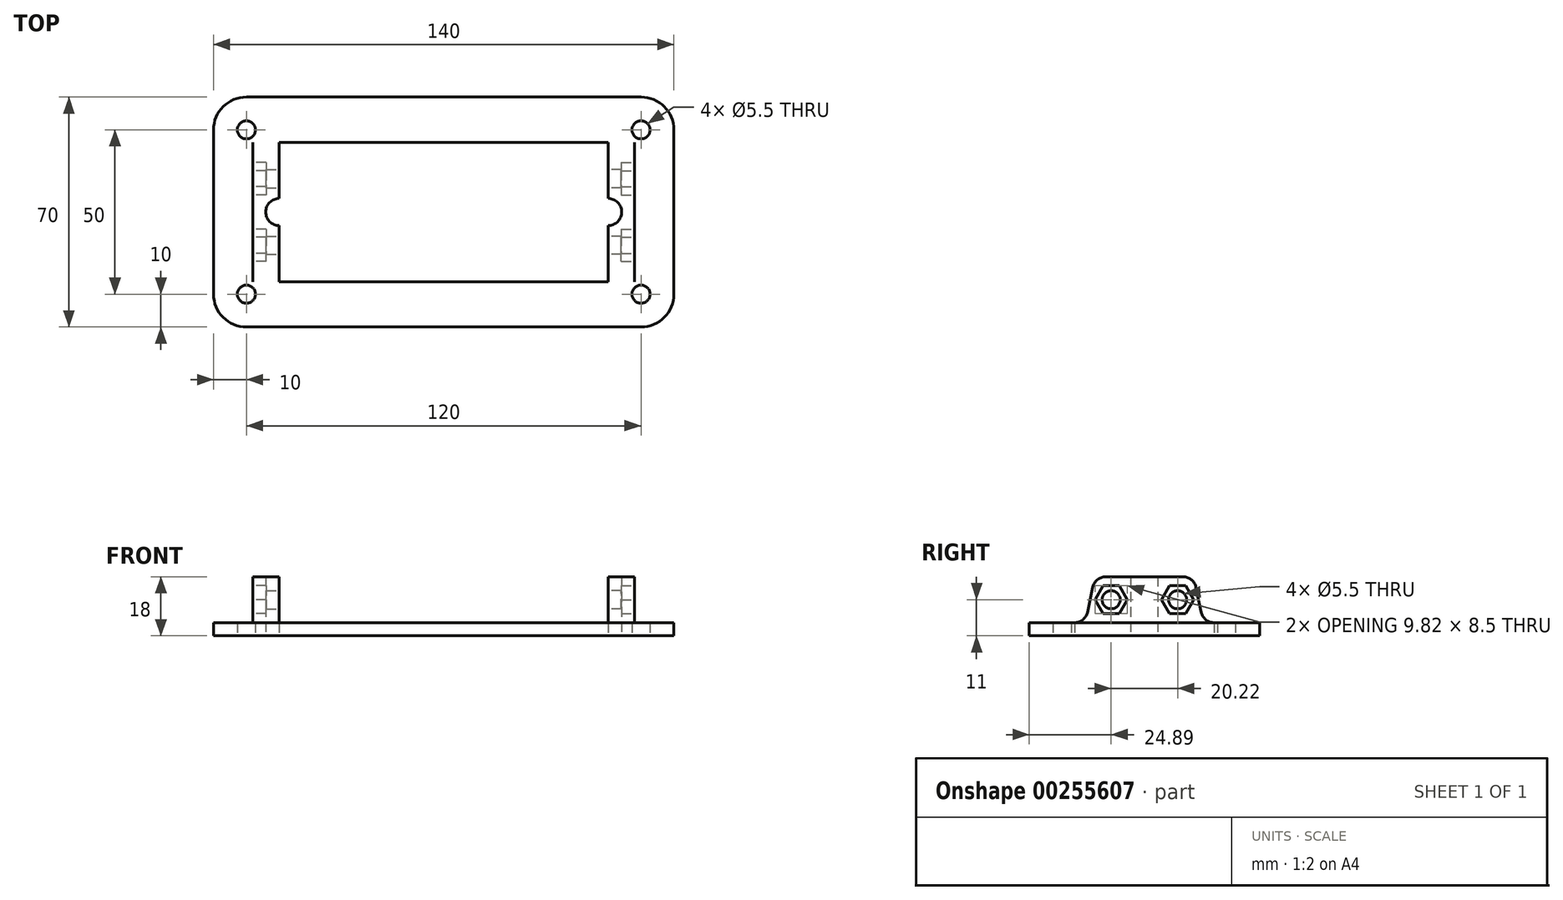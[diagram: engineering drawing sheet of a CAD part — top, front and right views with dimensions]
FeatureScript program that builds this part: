
annotation { "Feature Type Name" : "Feature", "Feature Type Description" : "" }
export const myFeature = defineFeature(function(context is Context, id is Id, definition is map)
    precondition{}
    {
        {
            var Q0;
            Q0=qCreatedBy(makeId("Top.planeOp"),FACE);
            var sketch = newSketch(context, id + "F0", { "sketchPlane" : qUnion([Q0])});
            skLineSegment(sketch, "E0.bottom", {"start": v(60, 35) * mm, "end": v(-60, 35) * mm});
            skLineSegment(sketch, "E0.top", {"start": v(60, -35) * mm, "end": v(-60, -35) * mm});
            skLineSegment(sketch, "E0.left", {"start": v(70, 25) * mm, "end": v(70, -25) * mm});
            skLineSegment(sketch, "E0.right", {"start": v(-70, 25) * mm, "end": v(-70, -25) * mm});
            skPoint(sketch, "E0.middle", {"position": v(0, 0) * mm});
            skLineSegment(sketch, "E1.bottom", {"start": v(50, 21.23) * mm, "end": v(-50, 21.23) * mm});
            skLineSegment(sketch, "E1.top", {"start": v(50, -21.23) * mm, "end": v(-50, -21.23) * mm});
            skLineSegment(sketch, "E1.left", {"start": v(50, 21.23) * mm, "end": v(50, -21.23) * mm});
            skLineSegment(sketch, "E1.right", {"start": v(-50, 21.23) * mm, "end": v(-50, -21.23) * mm});
            skLineSegment(sketch, "E2.bottom", {"start": v(-60, 25) * mm, "end": v(60, 25) * mm, "construction": true});
            skLineSegment(sketch, "E2.top", {"start": v(-60, -25) * mm, "end": v(60, -25) * mm, "construction": true});
            skLineSegment(sketch, "E2.left", {"start": v(-60, 25) * mm, "end": v(-60, -25) * mm, "construction": true});
            skLineSegment(sketch, "E2.right", {"start": v(60, 25) * mm, "end": v(60, -25) * mm, "construction": true});
            skCircle(sketch, "E3", {"center": v(-60, 25) * mm, "radius": 2.75 * mm});
            skCircle(sketch, "E4", {"center": v(60, 25) * mm, "radius": 2.75 * mm});
            skCircle(sketch, "E5", {"center": v(60, -25) * mm, "radius": 2.75 * mm});
            skCircle(sketch, "E6", {"center": v(-60, -25) * mm, "radius": 2.75 * mm});
            skPoint(sketch, "E7.visualSharp", {"position": v(-70, 35) * mm});
            skArc(sketch, "E7.filletArc", {"start": v(-60, 35) * mm, "mid": v(-67.07, 32.07) * mm, "end": v(-70, 25) * mm});
            skPoint(sketch, "E8.visualSharp", {"position": v(-70, -35) * mm});
            skArc(sketch, "E8.filletArc", {"start": v(-70, -25) * mm, "mid": v(-67.07, -32.07) * mm, "end": v(-60, -35) * mm});
            skPoint(sketch, "E9.visualSharp", {"position": v(70, -35) * mm});
            skArc(sketch, "E9.filletArc", {"start": v(60, -35) * mm, "mid": v(67.07, -32.07) * mm, "end": v(70, -25) * mm});
            skPoint(sketch, "E10.visualSharp", {"position": v(70, 35) * mm});
            skArc(sketch, "E10.filletArc", {"start": v(70, 25) * mm, "mid": v(67.07, 32.07) * mm, "end": v(60, 35) * mm});
            skSolve(sketch);
        }
        {
            var Q0;
            Q0=makeQuery(id+"F0.imprint","IMPRINT",FACE,{"disambiguationData":[TD([[makeQuery(id+"F0.imprint","IMPRINT",EDGE,{"derivedFrom":sQuery(id+"F0.wireOp",EDGE,"E0.bottom")}),1.0]])]});
            extrude(context, id + "F1", {"entities" : qUnion([Q0]), "depth" : 4 * mm});
        }
        {
            var Q0;
            Q0=makeQuery(id+"F1.opExtrude","SWEPT_FACE",FACE,{"disambiguationData":[OSD([sQuery(id+"F0.wireOp",EDGE,"E1.right")])]});
            var sketch = newSketch(context, id + "F2", { "sketchPlane" : qUnion([Q0])});
            skCircle(sketch, "E11", {"center": v(-10.11, 11) * mm, "radius": 2.75 * mm});
            skCircle(sketch, "E12.MirrorC", {"center": v(10.11, 11) * mm, "radius": 2.75 * mm});
            skArc(sketch, "E13", {"start": v(-21.24, 4) * mm, "mid": v(-18.72, 4.89) * mm, "end": v(-17.32, 7.16) * mm});
            skArc(sketch, "E14", {"start": v(-11.77, 18) * mm, "mid": v(-14.28, 17.11) * mm, "end": v(-15.68, 14.84) * mm});
            skLineSegment(sketch, "E15", {"start": v(-17.32, 7.16) * mm, "end": v(-15.68, 14.84) * mm});
            skLineSegment(sketch, "E16", {"start": v(-11.77, 18) * mm, "end": v(11.77, 18) * mm});
            skArc(sketch, "E17.MirrorCS", {"start": v(21.23, 4) * mm, "mid": v(18.72, 4.89) * mm, "end": v(17.32, 7.16) * mm});
            skLineSegment(sketch, "E18.MirrorCS", {"start": v(17.32, 7.16) * mm, "end": v(15.68, 14.84) * mm});
            skArc(sketch, "E19.MirrorCS", {"start": v(11.77, 18) * mm, "mid": v(14.28, 17.11) * mm, "end": v(15.68, 14.84) * mm});
            skSolve(sketch);
        }
        {
            var Q0;
            Q0=makeQuery(id+"F2.imprint","IMPRINT",FACE,{"disambiguationData":[TD([[makeQuery(id+"F2.imprint","IMPRINT",EDGE,{"derivedFrom":sQuery(id+"F2.wireOp",EDGE,"E11")}),-1.0]])]});
            extrude(context, id + "F3", {"entities" : qUnion([Q0]), "oppositeDirection" : true, "depth" : 8 * mm});
        }
        {
            var Q0;
            Q0=makeQuery(id+"F3.opExtrude","CAP_FACE",FACE,{"disambiguationData":[OSD([sQuery(id+"F0.wireOp",EDGE,"E1.right"),sQuery(id+"F2.wireOp",EDGE,"E11"),sQuery(id+"F2.wireOp",EDGE,"E12.MirrorC"),sQuery(id+"F2.wireOp",EDGE,"E13"),sQuery(id+"F2.wireOp",EDGE,"E14"),sQuery(id+"F2.wireOp",EDGE,"E15"),sQuery(id+"F2.wireOp",EDGE,"E16"),sQuery(id+"F2.wireOp",EDGE,"E17.MirrorCS"),sQuery(id+"F2.wireOp",EDGE,"E18.MirrorCS"),sQuery(id+"F2.wireOp",EDGE,"E19.MirrorCS")])],"isStart":false});
            var sketch = newSketch(context, id + "F4", { "sketchPlane" : qUnion([Q0])});
            skCircle(sketch, "E20.cCircle", {"center": v(-10.11, 11) * mm, "radius": 4.25 * mm, "construction": true});
            skLineSegment(sketch, "E20.0", {"start": v(-7.66, 15.25) * mm, "end": v(-5.2, 11) * mm});
            skLineSegment(sketch, "E20.1", {"start": v(-5.2, 11) * mm, "end": v(-7.66, 6.75) * mm});
            skLineSegment(sketch, "E20.2", {"start": v(-7.66, 6.75) * mm, "end": v(-12.56, 6.75) * mm});
            skLineSegment(sketch, "E20.3", {"start": v(-12.56, 6.75) * mm, "end": v(-15.02, 11) * mm});
            skLineSegment(sketch, "E20.4", {"start": v(-15.02, 11) * mm, "end": v(-12.56, 15.25) * mm});
            skLineSegment(sketch, "E20.5", {"start": v(-12.56, 15.25) * mm, "end": v(-7.66, 15.25) * mm});
            skPoint(sketch, "E20.0.midPoint", {"position": v(-6.43, 13.13) * mm});
            skCircle(sketch, "E21.cCircle", {"center": v(10.11, 11) * mm, "radius": 4.25 * mm, "construction": true});
            skLineSegment(sketch, "E21.0", {"start": v(12.56, 6.75) * mm, "end": v(7.66, 6.75) * mm});
            skLineSegment(sketch, "E21.1", {"start": v(7.66, 6.75) * mm, "end": v(5.2, 11) * mm});
            skLineSegment(sketch, "E21.2", {"start": v(5.2, 11) * mm, "end": v(7.66, 15.25) * mm});
            skLineSegment(sketch, "E21.3", {"start": v(7.66, 15.25) * mm, "end": v(12.56, 15.25) * mm});
            skLineSegment(sketch, "E21.4", {"start": v(12.56, 15.25) * mm, "end": v(15.02, 11) * mm});
            skLineSegment(sketch, "E21.5", {"start": v(15.02, 11) * mm, "end": v(12.56, 6.75) * mm});
            skPoint(sketch, "E21.0.midPoint", {"position": v(10.11, 6.75) * mm});
            skSolve(sketch);
        }
        {
            var Q0;
            Q0=makeQuery(id+"F4.imprint","IMPRINT",FACE,{"disambiguationData":[TD([[makeQuery(id+"F4.imprint","IMPRINT",EDGE,{"derivedFrom":sQuery(id+"F4.wireOp",EDGE,"E20.0")}),-1.0]])]});
            var Q1;
            Q1=makeQuery(id+"F4.imprint","IMPRINT",FACE,{"disambiguationData":[TD([[makeQuery(id+"F4.imprint","IMPRINT",EDGE,{"derivedFrom":sQuery(id+"F4.wireOp",EDGE,"E21.0")}),-1.0]])]});
            extrude(context, id + "F5", {"entities" : qUnion([Q0, Q1]), "operationType" : NewBodyOperationType.REMOVE, "oppositeDirection" : true, "depth" : 4 * mm});
        }
        {
            var Q0;
            Q0=makeQuery(id+"F3.opExtrude","SWEPT_BODY",BODY,{"disambiguationData":[OSD([sQuery(id+"F0.wireOp",EDGE,"E1.right"),sQuery(id+"F2.wireOp",EDGE,"E11"),sQuery(id+"F2.wireOp",EDGE,"E12.MirrorC"),sQuery(id+"F2.wireOp",EDGE,"E13"),sQuery(id+"F2.wireOp",EDGE,"E14"),sQuery(id+"F2.wireOp",EDGE,"E15"),sQuery(id+"F2.wireOp",EDGE,"E16"),sQuery(id+"F2.wireOp",EDGE,"E17.MirrorCS"),sQuery(id+"F2.wireOp",EDGE,"E18.MirrorCS"),sQuery(id+"F2.wireOp",EDGE,"E19.MirrorCS")])]});
            var Q1;
            Q1=qCreatedBy(makeId("Right.planeOp"),FACE);
            mirror(context, id + "F6", {"operationType" : NewBodyOperationType.ADD, "entities" : qUnion([Q0]), "mirrorPlane" : qUnion([Q1])});
        }
        {
            var Q0;
            Q0=makeQuery(id+"F1.opExtrude","CAP_FACE",FACE,{"disambiguationData":[OSD([sQuery(id+"F0.wireOp",EDGE,"E0.bottom"),sQuery(id+"F0.wireOp",EDGE,"E0.top"),sQuery(id+"F0.wireOp",EDGE,"E0.left"),sQuery(id+"F0.wireOp",EDGE,"E0.right"),sQuery(id+"F0.wireOp",EDGE,"E1.bottom"),sQuery(id+"F0.wireOp",EDGE,"E1.top"),sQuery(id+"F0.wireOp",EDGE,"E1.left"),sQuery(id+"F0.wireOp",EDGE,"E1.right"),sQuery(id+"F0.wireOp",EDGE,"E3"),sQuery(id+"F0.wireOp",EDGE,"E4"),sQuery(id+"F0.wireOp",EDGE,"E5"),sQuery(id+"F0.wireOp",EDGE,"E6"),sQuery(id+"F0.wireOp",EDGE,"E7.filletArc"),sQuery(id+"F0.wireOp",EDGE,"E8.filletArc"),sQuery(id+"F0.wireOp",EDGE,"E9.filletArc"),sQuery(id+"F0.wireOp",EDGE,"E10.filletArc")])],"isStart":true});
            var sketch = newSketch(context, id + "F7", { "sketchPlane" : qUnion([Q0])});
            skCircle(sketch, "E22", {"center": v(-50, 0) * mm, "radius": 4.12 * mm});
            skCircle(sketch, "E23", {"center": v(50, 0) * mm, "radius": 4.12 * mm});
            skSolve(sketch);
        }
        {
            var Q0;
            Q0 = qSketchRegion(id + "F7", true);
            extrude(context, id + "F8", {"entities" : qUnion([Q0]), "operationType" : NewBodyOperationType.REMOVE, "endBound" : BoundingType.THROUGH_ALL, "oppositeDirection" : true, "depth" : 25 * mm});
        }
    });
